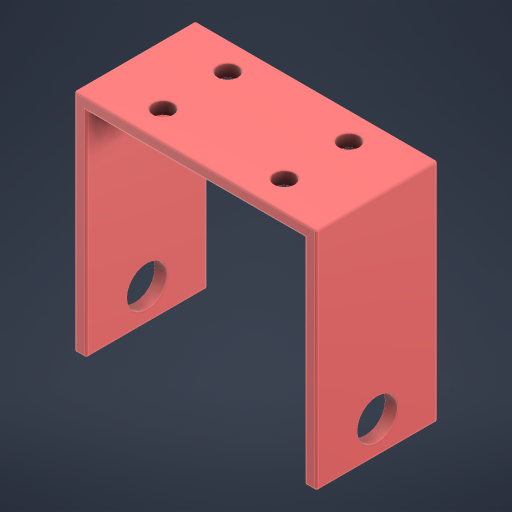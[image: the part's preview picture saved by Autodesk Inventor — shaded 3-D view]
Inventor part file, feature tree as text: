
AUTODESK INVENTOR PART (.ipt)
format: ipt  version: 2023 (Build 270158000, 158)  size: 243,712 bytes
history: native  units: mm
features: sketch x4, hole x3, extrude x1, fillet x1
ambient origin geometry x8: Origin, YZ Plane, XZ Plane, XY Plane, X Axis, Y Axis, Z Axis, Center Point
bodies: Solid1 (feature_tree)
feature tree (9):
  extrude  "Extrusion1"  Depth=56.0mm
  hole  "Hole1"  [1 undecoded]
  hole  "Hole2"  [1 undecoded]
  hole  "Hole3"  [1 undecoded]
  fillet  "Fillet1"  Radius=15.0mm
  sketch  "Sketch1"  dims[d2=3.0mm d4=56.0mm]
  sketch  "Sketch2"  dims[d5=53.0mm d6=30.0mm d7=0.0mm]
  sketch  "Sketch3"  dims[d8=45.0mm d9=15.0mm]
  sketch  "Sketch4"  dims[d10=10.0mm d11=6.0mm d12=4.0mm d13=2.0mm d14=90.0deg d15=8.0mm d16=20.594885mm d17=45.0mm d18=15.0mm d19=10.0mm d20=6.0mm d21=4.0mm d22=2.0mm d23=90.0deg d24=8.0mm d25=20.594885mm d26=7.0mm d27=15.0mm d28=7.0mm d29=15.0mm d30=7.0mm d31=15.0mm d32=15.0mm d33=7.0mm d34=5.0mm d35=6.0mm d36=4.0mm d37=2.0mm d38=90.0deg d39=8.0mm d40=20.594885mm d41=0.5mm]
note: 3 required parameter values undecoded (feature->parameter linkage not recoverable at this tier; creation-order binding heuristic only, values carry confidence <= 0.55)
